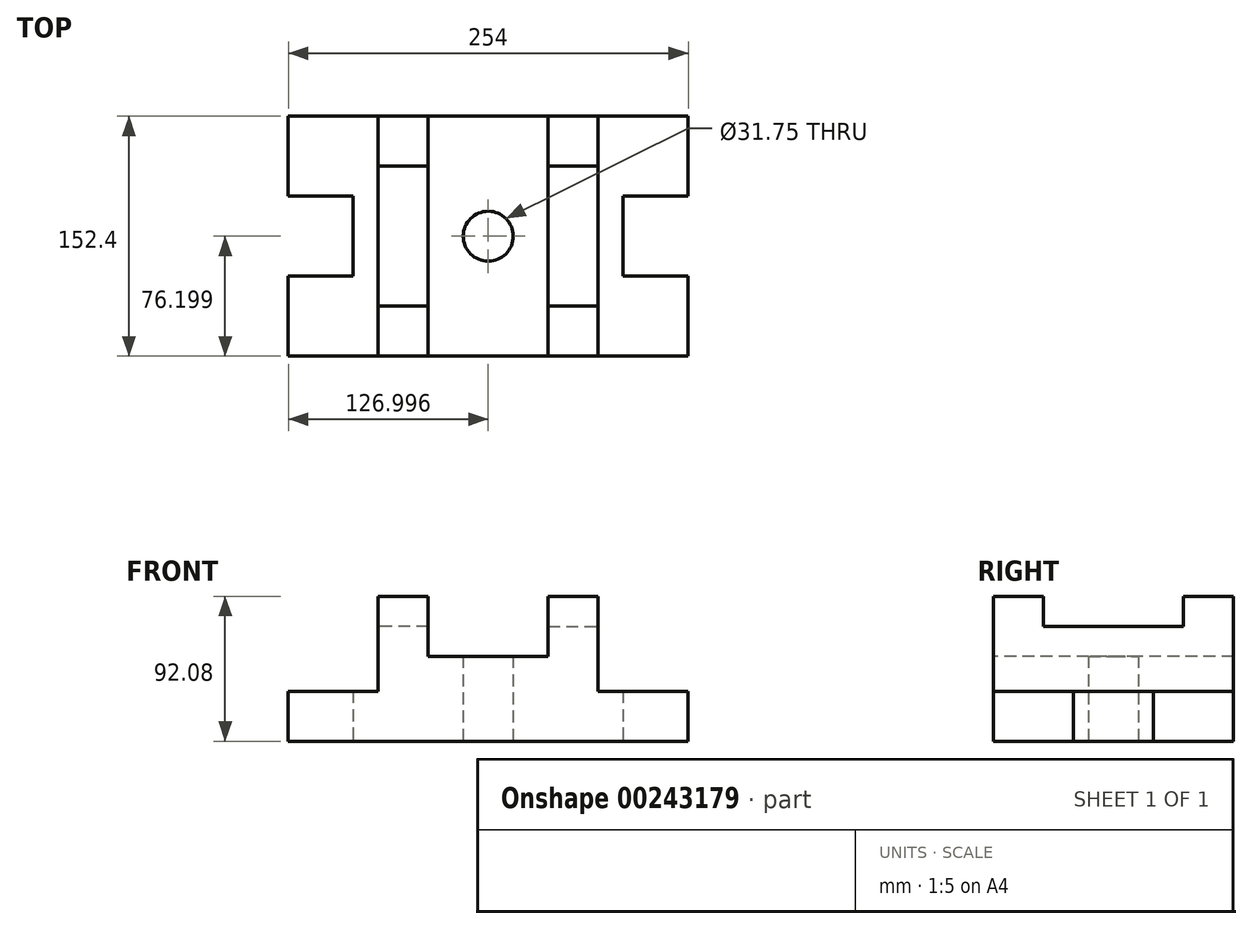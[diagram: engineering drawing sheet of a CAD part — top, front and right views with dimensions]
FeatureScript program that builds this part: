
annotation { "Feature Type Name" : "Feature", "Feature Type Description" : "" }
export const myFeature = defineFeature(function(context is Context, id is Id, definition is map)
    precondition{}
    {
        {
            var Q0;
            Q0=qCreatedBy(makeId("Top.planeOp"),FACE);
            var sketch = newSketch(context, id + "F0", { "sketchPlane" : qUnion([Q0])});
            skLineSegment(sketch, "E0.bottom", {"start": v(-13.85, 98.83) * mm, "end": v(43.3, 98.83) * mm});
            skLineSegment(sketch, "E0.top", {"start": v(-13.85, -53.57) * mm, "end": v(43.3, -53.57) * mm});
            skLineSegment(sketch, "E0.left", {"start": v(-13.85, 98.83) * mm, "end": v(-13.85, -53.57) * mm});
            skLineSegment(sketch, "E0.right", {"start": v(43.3, 98.83) * mm, "end": v(43.3, -53.57) * mm});
            skLineSegment(sketch, "E1", {"start": v(43.3, -2.77) * mm, "end": v(2.02, -2.77) * mm});
            skLineSegment(sketch, "E2", {"start": v(43.3, 48.03) * mm, "end": v(2.02, 48.03) * mm});
            skLineSegment(sketch, "E3", {"start": v(2.02, -2.77) * mm, "end": v(2.02, 48.03) * mm});
            skLineSegment(sketch, "E4.bottom", {"start": v(-45.6, 98.83) * mm, "end": v(-13.85, 98.83) * mm});
            skLineSegment(sketch, "E4.top", {"start": v(-45.6, -53.57) * mm, "end": v(-13.85, -53.57) * mm});
            skLineSegment(sketch, "E4.left", {"start": v(-45.6, 98.83) * mm, "end": v(-45.6, -53.57) * mm});
            skLineSegment(sketch, "E5", {"start": v(-45.6, 67.08) * mm, "end": v(-13.85, 67.08) * mm});
            skLineSegment(sketch, "E6", {"start": v(-45.6, -21.82) * mm, "end": v(-13.85, -21.82) * mm});
            skLineSegment(sketch, "E7.bottom", {"start": v(-45.6, 98.83) * mm, "end": v(-83.7, 98.83) * mm});
            skLineSegment(sketch, "E7.top", {"start": v(-45.6, -53.57) * mm, "end": v(-83.7, -53.57) * mm});
            skLineSegment(sketch, "E7.right", {"start": v(-83.7, 98.83) * mm, "end": v(-83.7, -53.57) * mm});
            skLineSegment(sketch, "E8.MirrorCS", {"start": v(-121.8, 98.83) * mm, "end": v(-121.8, -53.57) * mm});
            skLineSegment(sketch, "E9.MirrorCS", {"start": v(-153.55, 98.83) * mm, "end": v(-153.55, -53.57) * mm});
            skLineSegment(sketch, "E10.MirrorCS", {"start": v(-121.8, -53.57) * mm, "end": v(-153.55, -53.57) * mm});
            skCircle(sketch, "E11.MirrorC", {"center": v(-83.7, 22.63) * mm, "radius": 15.88 * mm});
            skLineSegment(sketch, "E12.MirrorCS", {"start": v(-121.8, 98.83) * mm, "end": v(-83.7, 98.83) * mm});
            skLineSegment(sketch, "E13.MirrorCS", {"start": v(-121.8, -21.82) * mm, "end": v(-153.55, -21.82) * mm});
            skLineSegment(sketch, "E14.MirrorCS", {"start": v(-121.8, 98.83) * mm, "end": v(-153.55, 98.83) * mm});
            skLineSegment(sketch, "E15.MirrorCS", {"start": v(-169.43, -2.77) * mm, "end": v(-169.43, 48.03) * mm});
            skLineSegment(sketch, "E16.MirrorCS", {"start": v(-210.7, 98.83) * mm, "end": v(-210.7, -53.57) * mm});
            skLineSegment(sketch, "E17.MirrorCS", {"start": v(-121.8, 67.08) * mm, "end": v(-153.55, 67.08) * mm});
            skLineSegment(sketch, "E18.MirrorCS", {"start": v(-121.8, -53.57) * mm, "end": v(-83.7, -53.57) * mm});
            skLineSegment(sketch, "E19.MirrorCS", {"start": v(-210.7, -2.77) * mm, "end": v(-169.43, -2.77) * mm});
            skLineSegment(sketch, "E20.MirrorCS", {"start": v(-210.7, 48.03) * mm, "end": v(-169.43, 48.03) * mm});
            skLineSegment(sketch, "E21.MirrorCS", {"start": v(-153.55, -53.57) * mm, "end": v(-210.7, -53.57) * mm});
            skLineSegment(sketch, "E22.MirrorCS", {"start": v(-153.55, 98.83) * mm, "end": v(-210.7, 98.83) * mm});
            skSolve(sketch);
        }
        {
            var Q0;
            Q0=makeQuery(id+"F0.imprint","IMPRINT",FACE,{"disambiguationData":[TD([[makeQuery(id+"F0.imprint","IMPRINT",EDGE,{"derivedFrom":sQuery(id+"F0.wireOp",EDGE,"E15.MirrorCS")}),-1.0]])]});
            var Q1;
            {var subQ3=sQuery(id+"F0.wireOp",EDGE,"E0.bottom");Q1=makeQuery(id+"F0.imprint","IMPRINT",FACE,{"disambiguationData":[TD([[makeQuery(id+"F0.imprint","IMPRINT",EDGE,{"derivedFrom":subQ3}),-1.0]])]});}
            extrude(context, id + "F1", {"entities" : qUnion([Q0, Q1]), "depth" : 31.75 * mm});
        }
        {
            var Q0;
            {var subQ0=sQuery(id+"F0.wireOp",EDGE,"E14.MirrorCS");Q0=makeQuery(id+"F0.imprint","IMPRINT",FACE,{"disambiguationData":[TD([[makeQuery(id+"F0.imprint","IMPRINT",EDGE,{"derivedFrom":subQ0}),1.0]])]});}
            var Q1;
            {var subQ0=sQuery(id+"F0.wireOp",EDGE,"E10.MirrorCS");Q1=makeQuery(id+"F0.imprint","IMPRINT",FACE,{"disambiguationData":[TD([[makeQuery(id+"F0.imprint","IMPRINT",EDGE,{"derivedFrom":subQ0}),-1.0]])]});}
            var Q2;
            {var subQ0=sQuery(id+"F0.wireOp",EDGE,"E4.top");Q2=makeQuery(id+"F0.imprint","IMPRINT",FACE,{"disambiguationData":[TD([[makeQuery(id+"F0.imprint","IMPRINT",EDGE,{"derivedFrom":subQ0}),1.0]])]});}
            var Q3;
            {var subQ0=sQuery(id+"F0.wireOp",EDGE,"E4.bottom");Q3=makeQuery(id+"F0.imprint","IMPRINT",FACE,{"disambiguationData":[TD([[makeQuery(id+"F0.imprint","IMPRINT",EDGE,{"derivedFrom":subQ0}),-1.0]])]});}
            extrude(context, id + "F2", {"entities" : qUnion([Q0, Q1, Q2, Q3]), "operationType" : NewBodyOperationType.ADD, "depth" : 92.07 * mm});
        }
        {
            var Q0;
            {var subQ0=sQuery(id+"F0.wireOp",EDGE,"E13.MirrorCS");Q0=makeQuery(id+"F0.imprint","IMPRINT",FACE,{"disambiguationData":[TD([[makeQuery(id+"F0.imprint","IMPRINT",EDGE,{"derivedFrom":subQ0}),-1.0]])]});}
            var Q1;
            {var subQ0=sQuery(id+"F0.wireOp",EDGE,"E5");Q1=makeQuery(id+"F0.imprint","IMPRINT",FACE,{"disambiguationData":[TD([[makeQuery(id+"F0.imprint","IMPRINT",EDGE,{"derivedFrom":subQ0}),-1.0]])]});}
            extrude(context, id + "F3", {"entities" : qUnion([Q0, Q1]), "operationType" : NewBodyOperationType.ADD, "depth" : 73.02 * mm});
        }
        {
            var Q0;
            {var subQ0=sQuery(id+"F0.wireOp",EDGE,"E12.MirrorCS");Q0=makeQuery(id+"F0.imprint","IMPRINT",FACE,{"disambiguationData":[TD([[makeQuery(id+"F0.imprint","IMPRINT",EDGE,{"derivedFrom":subQ0}),-1.0]])]});}
            var Q1;
            {var subQ3=sQuery(id+"F0.wireOp",EDGE,"E7.bottom");Q1=makeQuery(id+"F0.imprint","IMPRINT",FACE,{"disambiguationData":[TD([[makeQuery(id+"F0.imprint","IMPRINT",EDGE,{"derivedFrom":subQ3}),1.0]])]});}
            extrude(context, id + "F4", {"entities" : qUnion([Q0, Q1]), "operationType" : NewBodyOperationType.ADD, "depth" : 53.97 * mm});
        }
    });
